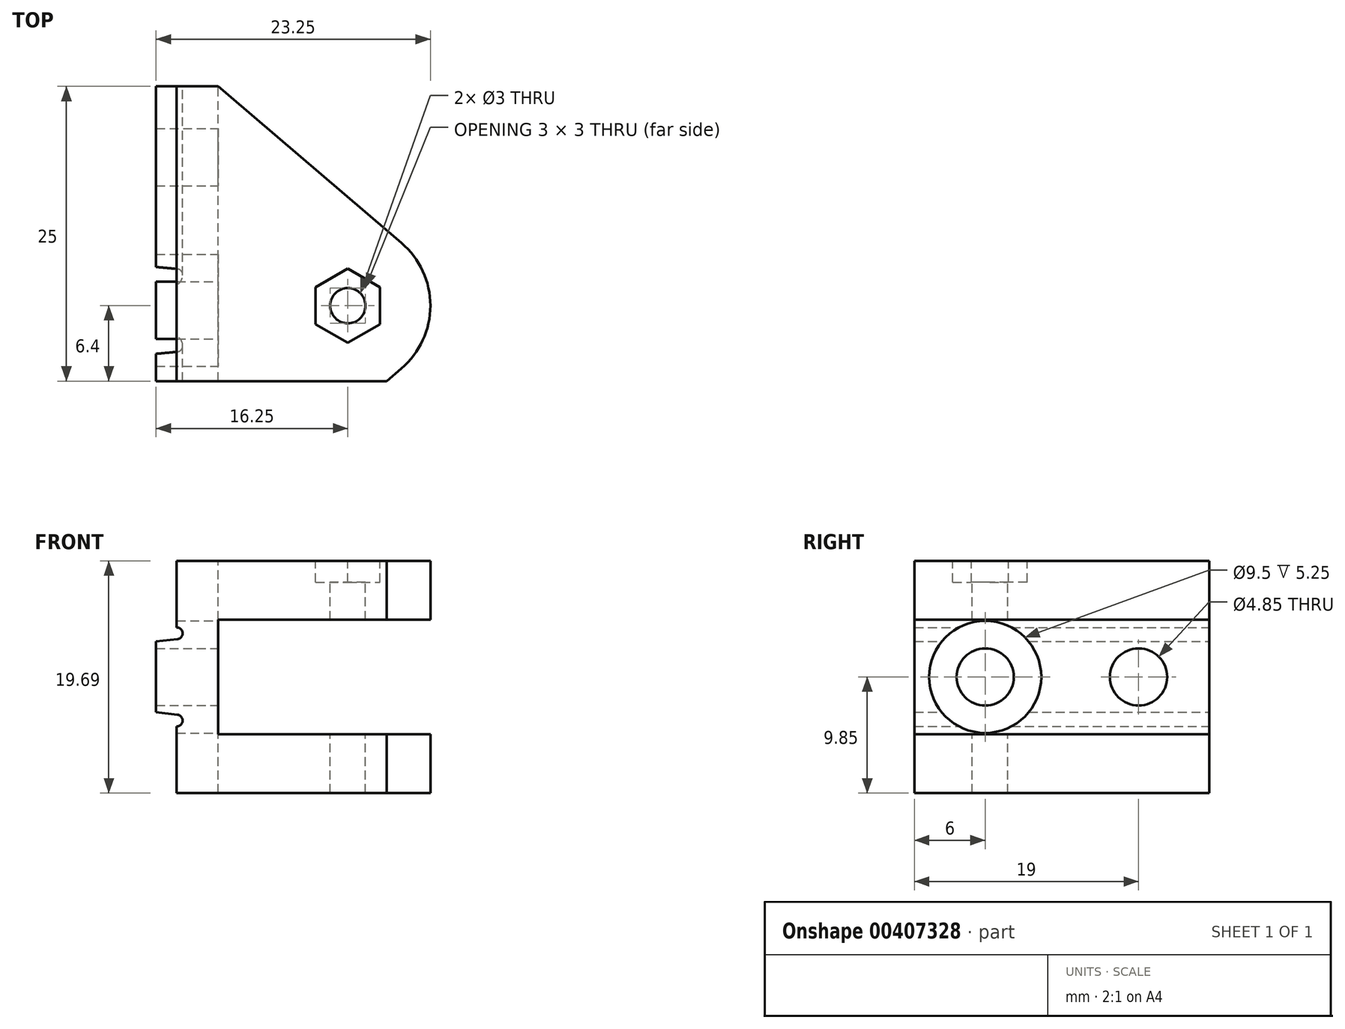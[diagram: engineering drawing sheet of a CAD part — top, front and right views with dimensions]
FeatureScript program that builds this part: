
annotation { "Feature Type Name" : "Feature", "Feature Type Description" : "" }
export const myFeature = defineFeature(function(context is Context, id is Id, definition is map)
    precondition{}
    {
        {
            var Q0;
            Q0=qCreatedBy(makeId("Front.planeOp"),FACE);
            var sketch = newSketch(context, id + "F0", { "sketchPlane" : qUnion([Q0])});
            skLineSegment(sketch, "E0", {"start": v(5.5, -9.85) * mm, "end": v(2, -9.85) * mm});
            skLineSegment(sketch, "E1", {"start": v(2, -9.85) * mm, "end": v(2, -4.2) * mm});
            skLineSegment(sketch, "E2", {"start": v(2.06, -3.2) * mm, "end": v(0.25, -3) * mm});
            skLineSegment(sketch, "E3", {"start": v(0, 0) * mm, "end": v(11.01, 0) * mm, "construction": true});
            skLineSegment(sketch, "E4", {"start": v(2, -10) * mm, "end": v(2, -3.1) * mm, "construction": true});
            skLineSegment(sketch, "E5", {"start": v(2, -3.1) * mm, "end": v(0, -3.1) * mm, "construction": true});
            skLineSegment(sketch, "E6", {"start": v(0, -3.1) * mm, "end": v(0, 0) * mm, "construction": true});
            skLineSegment(sketch, "E7", {"start": v(2, -10) * mm, "end": v(-1.72, -10) * mm, "construction": true});
            skLineSegment(sketch, "E8.MirrorCS", {"start": v(0, 3.1) * mm, "end": v(0, 0) * mm, "construction": true});
            skLineSegment(sketch, "E9.MirrorCS", {"start": v(2, 3.1) * mm, "end": v(0, 3.1) * mm, "construction": true});
            skLineSegment(sketch, "E10.MirrorCS", {"start": v(2, 10) * mm, "end": v(2, 3.1) * mm, "construction": true});
            skLineSegment(sketch, "E11.MirrorCS", {"start": v(2, 10) * mm, "end": v(-1.72, 10) * mm, "construction": true});
            skArc(sketch, "E12", {"start": v(2.06, -3.2) * mm, "mid": v(2.5, -3.72) * mm, "end": v(2, -4.2) * mm});
            skLineSegment(sketch, "E13", {"start": v(0.25, -3) * mm, "end": v(0.25, 3) * mm});
            skLineSegment(sketch, "E14.MirrorCS", {"start": v(2.06, 3.2) * mm, "end": v(0.25, 3) * mm});
            skArc(sketch, "E15.MirrorCS", {"start": v(2.06, 3.2) * mm, "mid": v(2.5, 3.72) * mm, "end": v(2, 4.2) * mm});
            skLineSegment(sketch, "E16.MirrorCS", {"start": v(2, 9.85) * mm, "end": v(2, 4.2) * mm});
            skLineSegment(sketch, "E17.MirrorCS", {"start": v(5.5, 9.84) * mm, "end": v(2, 9.84) * mm});
            skLineSegment(sketch, "E18", {"start": v(10.77, -4.23) * mm, "end": v(22.23, -4.22) * mm, "construction": true});
            skLineSegment(sketch, "E19", {"start": v(22.24, -4.22) * mm, "end": v(22.24, -3.22) * mm, "construction": true});
            skLineSegment(sketch, "E20", {"start": v(22.23, -3.22) * mm, "end": v(10.77, -3.23) * mm, "construction": true});
            skLineSegment(sketch, "E21", {"start": v(10.77, -3.22) * mm, "end": v(10.77, -4.23) * mm, "construction": true});
            skLineSegment(sketch, "E22", {"start": v(21.5, -3.22) * mm, "end": v(21.5, -0.24) * mm, "construction": true});
            skLineSegment(sketch, "E23", {"start": v(21.5, -0.24) * mm, "end": v(11.5, -0.25) * mm, "construction": true});
            skLineSegment(sketch, "E24", {"start": v(11.5, -0.25) * mm, "end": v(11.5, -3.23) * mm, "construction": true});
            skLineSegment(sketch, "E25", {"start": v(16.5, -0.24) * mm, "end": v(16.5, -3.22) * mm, "construction": true});
            skLineSegment(sketch, "E26", {"start": v(16.5, -3.22) * mm, "end": v(16.5, -4.22) * mm, "construction": true});
            skLineSegment(sketch, "E27.MirrorCS", {"start": v(21.5, 0.25) * mm, "end": v(11.5, 0.24) * mm, "construction": true});
            skLineSegment(sketch, "E28.MirrorCS", {"start": v(16.5, 0.24) * mm, "end": v(16.5, 3.22) * mm, "construction": true});
            skLineSegment(sketch, "E29.MirrorCS", {"start": v(11.5, 0.24) * mm, "end": v(11.5, 3.22) * mm, "construction": true});
            skLineSegment(sketch, "E30.MirrorCS", {"start": v(22.23, 3.23) * mm, "end": v(10.77, 3.22) * mm, "construction": true});
            skLineSegment(sketch, "E31.MirrorCS", {"start": v(10.76, 3.22) * mm, "end": v(10.76, 4.22) * mm, "construction": true});
            skLineSegment(sketch, "E32.MirrorCS", {"start": v(10.76, 4.23) * mm, "end": v(22.23, 4.22) * mm, "construction": true});
            skLineSegment(sketch, "E33.MirrorCS", {"start": v(22.24, 4.22) * mm, "end": v(22.24, 3.22) * mm, "construction": true});
            skLineSegment(sketch, "E34.MirrorCS", {"start": v(21.5, 3.22) * mm, "end": v(21.5, 0.24) * mm, "construction": true});
            skLineSegment(sketch, "E35.MirrorCS", {"start": v(16.5, 3.22) * mm, "end": v(16.5, 4.22) * mm, "construction": true});
            skLineSegment(sketch, "E36", {"start": v(5.5, -9.84) * mm, "end": v(5.5, 9.84) * mm});
            skLineSegment(sketch, "E37", {"start": v(10.1, -3.23) * mm, "end": v(10.1, 3.23) * mm, "construction": true});
            skArc(sketch, "E38", {"start": v(6.4, -4.65) * mm, "mid": v(8.9, 0) * mm, "end": v(6.4, 4.65) * mm, "construction": true});
            skLineSegment(sketch, "E39", {"start": v(6.4, -4.65) * mm, "end": v(6.4, 4.65) * mm, "construction": true});
            skLineSegment(sketch, "E40", {"start": v(6.4, 0) * mm, "end": v(8.9, 0) * mm, "construction": true});
            skLineSegment(sketch, "E41", {"start": v(5.5, -4.84) * mm, "end": v(23.5, -4.84) * mm});
            skLineSegment(sketch, "E42", {"start": v(23.5, -4.84) * mm, "end": v(23.5, -9.84) * mm});
            skLineSegment(sketch, "E43", {"start": v(23.5, -9.84) * mm, "end": v(5.5, -9.84) * mm});
            skLineSegment(sketch, "E44.MirrorCS", {"start": v(5.5, 4.84) * mm, "end": v(23.5, 4.84) * mm});
            skLineSegment(sketch, "E45.MirrorCS", {"start": v(23.5, 4.84) * mm, "end": v(23.5, 9.84) * mm});
            skLineSegment(sketch, "E46.MirrorCS", {"start": v(23.5, 9.85) * mm, "end": v(5.5, 9.84) * mm});
            skLineSegment(sketch, "E47", {"start": v(15.03, -4.85) * mm, "end": v(15.03, -9.85) * mm, "construction": true});
            skLineSegment(sketch, "E48.MirrorCS", {"start": v(17.98, -4.84) * mm, "end": v(17.98, -9.85) * mm, "construction": true});
            skLineSegment(sketch, "E49", {"start": v(10.77, -4.23) * mm, "end": v(10.77, 4.22) * mm});
            skLineSegment(sketch, "E50", {"start": v(10.77, -4.23) * mm, "end": v(22.23, -4.22) * mm});
            skLineSegment(sketch, "E51", {"start": v(22.24, -4.31) * mm, "end": v(22.24, 4.22) * mm});
            skLineSegment(sketch, "E52", {"start": v(22.23, 4.22) * mm, "end": v(10.76, 4.22) * mm});
            skLineSegment(sketch, "E53", {"start": v(20.5, 4.23) * mm, "end": v(20.5, 4.74) * mm});
            skLineSegment(sketch, "E54.MirrorCS", {"start": v(12.5, 4.23) * mm, "end": v(12.5, 4.74) * mm});
            skLineSegment(sketch, "E55.MirrorCS", {"start": v(20.5, -4.22) * mm, "end": v(20.5, -4.74) * mm});
            skLineSegment(sketch, "E56.MirrorCS", {"start": v(12.5, -4.23) * mm, "end": v(12.5, -4.74) * mm});
            skLineSegment(sketch, "E57", {"start": v(20.5, 4.74) * mm, "end": v(12.5, 4.74) * mm});
            skLineSegment(sketch, "E58.MirrorCS", {"start": v(20.5, -4.74) * mm, "end": v(12.5, -4.74) * mm});
            skSolve(sketch);
        }
        {
            var Q0;
            {var subQ1=sQuery(id+"F0.wireOp",EDGE,"E0");Q0=makeQuery(id+"F0.imprint","IMPRINT",FACE,{"disambiguationData":[TD([[makeQuery(id+"F0.imprint","IMPRINT",EDGE,{"derivedFrom":subQ1}),-1.0]])]});}
            var Q1;
            {var subQ2=sQuery(id+"F0.wireOp",EDGE,"E41");Q1=makeQuery(id+"F0.imprint","IMPRINT",FACE,{"disambiguationData":[TD([[makeQuery(id+"F0.imprint","IMPRINT",EDGE,{"derivedFrom":subQ2}),-1.0]])]});}
            var Q2;
            {var subQ2=sQuery(id+"F0.wireOp",EDGE,"E44.MirrorCS");Q2=makeQuery(id+"F0.imprint","IMPRINT",FACE,{"disambiguationData":[TD([[makeQuery(id+"F0.imprint","IMPRINT",EDGE,{"derivedFrom":subQ2}),1.0]])]});}
            extrude(context, id + "F1", {"entities" : qUnion([Q0, Q1, Q2]), "depth" : 25 * mm});
        }
        {
            var Q0;
            Q0=makeQuery(id+"F1.opExtrude","SWEPT_FACE",FACE,{"disambiguationData":[OSD([sQuery(id+"F0.wireOp",EDGE,"E44.MirrorCS")])]});
            var sketch = newSketch(context, id + "F2", { "sketchPlane" : qUnion([Q0])});
            skLineSegment(sketch, "E59", {"start": v(19.78, 25) * mm, "end": v(21.05, 23.92) * mm});
            skLineSegment(sketch, "E60", {"start": v(5.5, 0) * mm, "end": v(21.05, 13.28) * mm});
            skArc(sketch, "E61", {"start": v(21.05, 23.92) * mm, "mid": v(23.5, 18.6) * mm, "end": v(21.05, 13.28) * mm});
            skCircle(sketch, "E62", {"center": v(16.5, 18.6) * mm, "radius": 5 * mm, "construction": true});
            skLineSegment(sketch, "E63", {"start": v(16.5, 23.6) * mm, "end": v(5.5, 23.6) * mm, "construction": true});
            skLineSegment(sketch, "E64.0", {"start": v(5.5, 25) * mm, "end": v(23.5, 25) * mm, "construction": true});
            skCircle(sketch, "E65", {"center": v(16.5, 18.6) * mm, "radius": 1.5 * mm});
            skLineSegment(sketch, "E66", {"start": v(19.78, 25) * mm, "end": v(5.5, 25) * mm});
            skLineSegment(sketch, "E67.0", {"start": v(23.5, 25) * mm, "end": v(23.5, 0) * mm, "construction": true});
            skLineSegment(sketch, "E68", {"start": v(21.05, 13.28) * mm, "end": v(21.05, 23.92) * mm, "construction": true});
            skCircle(sketch, "E69", {"center": v(16.5, 18.6) * mm, "radius": 5.73 * mm, "construction": true});
            skLineSegment(sketch, "E70", {"start": v(5.5, 25) * mm, "end": v(5.5, 0) * mm, "construction": true});
            skLineSegment(sketch, "E71", {"start": v(16.5, 18.6) * mm, "end": v(16.5, 2.46) * mm, "construction": true});
            skSolve(sketch);
        }
        {
            var Q0;
            {var subQ0=sQuery(id+"F2.wireOp",EDGE,"E59");Q0=makeQuery(id+"F2.imprint","IMPRINT",FACE,{"disambiguationData":[TD([[makeQuery(id+"F2.imprint","IMPRINT",EDGE,{"derivedFrom":subQ0}),1.0]])]});}
            var Q1;
            {var subQ0=sQuery(id+"F2.wireOp",EDGE,"E60");Q1=makeQuery(id+"F2.imprint","IMPRINT",FACE,{"disambiguationData":[TD([[makeQuery(id+"F2.imprint","IMPRINT",EDGE,{"derivedFrom":subQ0}),-1.0]])]});}
            var Q2;
            Q2=makeQuery(id+"F2.imprint","IMPRINT",FACE,{"disambiguationData":[TD([[makeQuery(id+"F2.imprint","IMPRINT",EDGE,{"derivedFrom":sQuery(id+"F2.wireOp",EDGE,"E65")}),1.0]])]});
            extrude(context, id + "F3", {"entities" : qUnion([Q0, Q1, Q2]), "operationType" : NewBodyOperationType.REMOVE, "endBound" : BoundingType.THROUGH_ALL, "depth" : 25 * mm, "hasSecondDirection" : true, "secondDirectionOppositeDirection" : true, "secondDirectionDepth" : 25 * mm});
        }
        {
            var Q0;
            Q0=makeQuery(id+"F1.opExtrude","SWEPT_FACE",FACE,{"disambiguationData":[OSD([sQuery(id+"F0.wireOp",EDGE,"E44.MirrorCS")])]});
            var sketch = newSketch(context, id + "F4", { "sketchPlane" : qUnion([Q0])});
            skCircle(sketch, "E72.0", {"center": v(16.5, 18.6) * mm, "radius": 1.5 * mm});
            skCircle(sketch, "E73", {"center": v(16.5, 18.6) * mm, "radius": 3.5 * mm});
            skSolve(sketch);
        }
        {
            var Q0;
            Q0=makeQuery(id+"F0.imprint","IMPRINT",FACE,{"disambiguationData":[TD([[makeQuery(id+"F0.imprint","IMPRINT",EDGE,{"derivedFrom":sQuery(id+"F0.wireOp",EDGE,"E49")}),-1.0]])]});
            var Q1;
            {var subQ0=sQuery(id+"F0.wireOp",EDGE,"E53");Q1=makeQuery(id+"F0.imprint","IMPRINT",FACE,{"disambiguationData":[TD([[makeQuery(id+"F0.imprint","IMPRINT",EDGE,{"derivedFrom":subQ0}),1.0]])]});}
            var Q2;
            {var subQ0=sQuery(id+"F0.wireOp",EDGE,"E55.MirrorCS");Q2=makeQuery(id+"F0.imprint","IMPRINT",FACE,{"disambiguationData":[TD([[makeQuery(id+"F0.imprint","IMPRINT",EDGE,{"derivedFrom":subQ0}),-1.0]])]});}
            extrude(context, id + "F5", {"entities" : qUnion([Q0, Q1, Q2]), "operationType" : NewBodyOperationType.REMOVE, "depth" : 25 * mm});
        }
        {
            var Q0;
            Q0=makeQuery(id+"F1.opExtrude","SWEPT_FACE",FACE,{"disambiguationData":[OSD([sQuery(id+"F0.wireOp",EDGE,"E36")])]});
            var sketch = newSketch(context, id + "F6", { "sketchPlane" : qUnion([Q0])});
            skLineSegment(sketch, "E74.0", {"start": v(0, -4.84) * mm, "end": v(0, 4.85) * mm});
            skLineSegment(sketch, "E75.0", {"start": v(-25, -4.84) * mm, "end": v(-25, 4.84) * mm});
            skLineSegment(sketch, "E76", {"start": v(0, 0) * mm, "end": v(-25, 0) * mm, "construction": true});
            skCircle(sketch, "E77", {"center": v(-6, 0) * mm, "radius": 4.75 * mm});
            skLineSegment(sketch, "E78", {"start": v(-12.5, 0) * mm, "end": v(-12.5, -3.12) * mm, "construction": true});
            skCircle(sketch, "E79.MirrorC", {"center": v(-19, 0) * mm, "radius": 4.75 * mm});
            skCircle(sketch, "E80", {"center": v(-6, 0) * mm, "radius": 2.43 * mm});
            skCircle(sketch, "E81.MirrorC", {"center": v(-19, 0) * mm, "radius": 2.43 * mm});
            skSolve(sketch);
        }
        {
            var Q0;
            Q0=makeQuery(id+"F6.imprint","IMPRINT",FACE,{"disambiguationData":[TD([[makeQuery(id+"F6.imprint","IMPRINT",EDGE,{"derivedFrom":sQuery(id+"F6.wireOp",EDGE,"E80")}),1.0]])]});
            var Q1;
            Q1=makeQuery(id+"F6.imprint","IMPRINT",FACE,{"disambiguationData":[TD([[makeQuery(id+"F6.imprint","IMPRINT",EDGE,{"derivedFrom":sQuery(id+"F6.wireOp",EDGE,"E81.MirrorC")}),-1.0]])]});
            extrude(context, id + "F7", {"entities" : qUnion([Q0, Q1]), "operationType" : NewBodyOperationType.REMOVE, "oppositeDirection" : true, "depth" : 25 * mm});
        }
        {
            var Q0;
            Q0=makeQuery(id+"F1.opExtrude","SWEPT_FACE",FACE,{"disambiguationData":[OSD([sQuery(id+"F0.wireOp",EDGE,"E17.MirrorCS"),sQuery(id+"F0.wireOp",EDGE,"E46.MirrorCS")])]});
            var sketch = newSketch(context, id + "F8", { "sketchPlane" : qUnion([Q0])});
            skCircle(sketch, "E82.cCircle", {"center": v(16.5, -18.6) * mm, "radius": 3.15 * mm, "construction": true});
            skLineSegment(sketch, "E82.0", {"start": v(19.22, -17.03) * mm, "end": v(19.22, -20.17) * mm});
            skLineSegment(sketch, "E82.1", {"start": v(19.22, -20.17) * mm, "end": v(16.5, -21.75) * mm});
            skLineSegment(sketch, "E82.2", {"start": v(16.5, -21.75) * mm, "end": v(13.77, -20.17) * mm});
            skLineSegment(sketch, "E82.3", {"start": v(13.77, -20.17) * mm, "end": v(13.77, -17.03) * mm});
            skLineSegment(sketch, "E82.4", {"start": v(13.77, -17.03) * mm, "end": v(16.5, -15.45) * mm});
            skLineSegment(sketch, "E82.5", {"start": v(16.5, -15.45) * mm, "end": v(19.22, -17.03) * mm});
            skCircle(sketch, "E83.0", {"center": v(16.5, -18.6) * mm, "radius": 1.5 * mm, "construction": true});
            skSolve(sketch);
        }
        {
            var Q0;
            Q0=makeQuery(id+"F8.imprint","IMPRINT",FACE,{"disambiguationData":[TD([[makeQuery(id+"F8.imprint","IMPRINT",EDGE,{"derivedFrom":sQuery(id+"F8.wireOp",EDGE,"E82.0")}),-1.0]])]});
            extrude(context, id + "F9", {"entities" : qUnion([Q0]), "operationType" : NewBodyOperationType.REMOVE, "oppositeDirection" : true, "depth" : 1.8 * mm});
        }
    });
